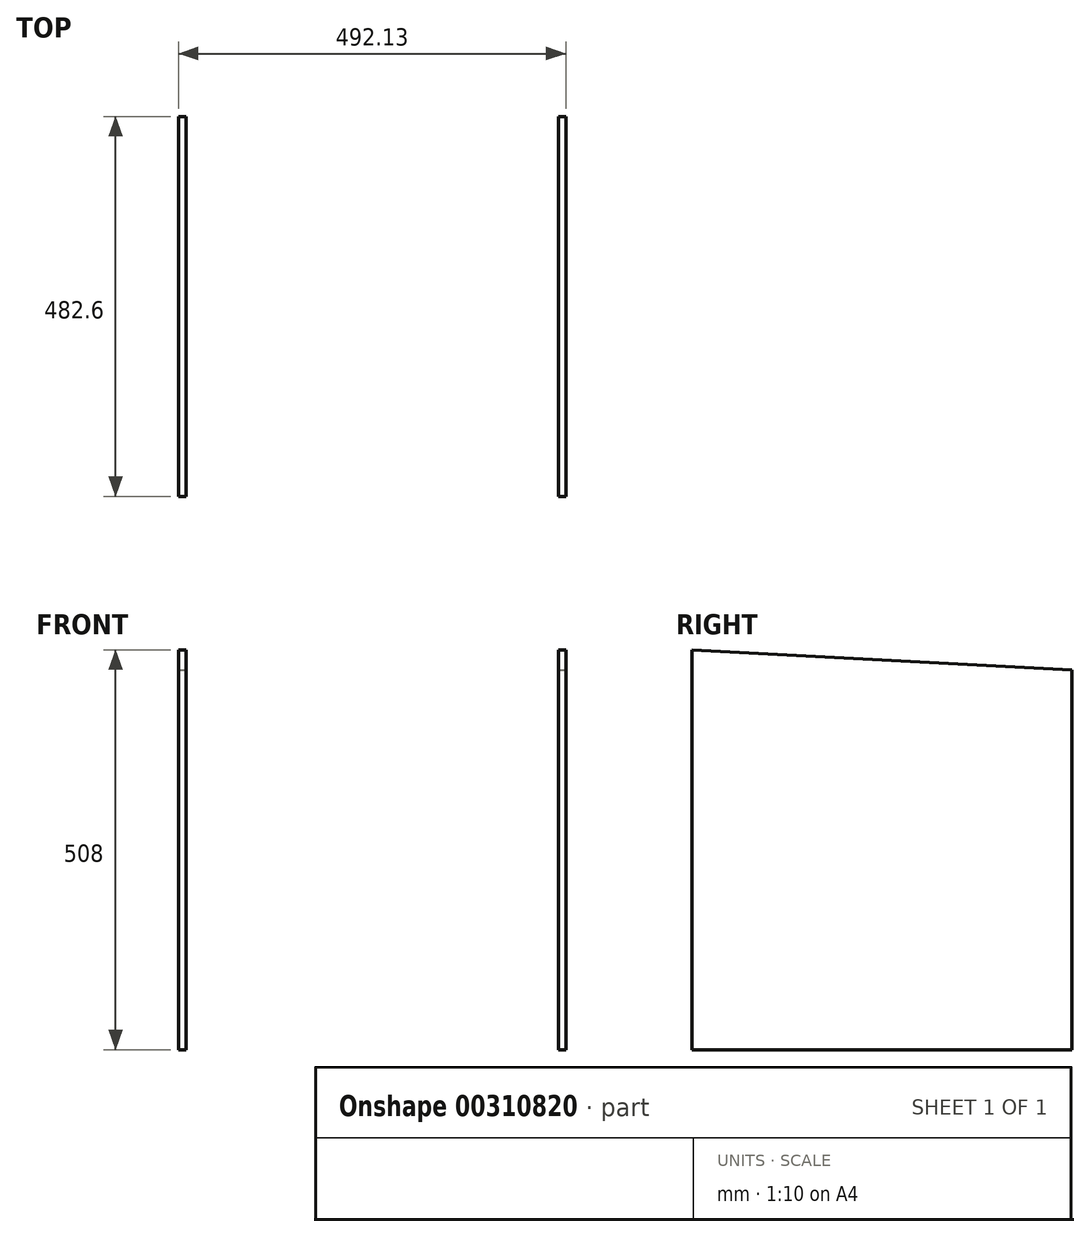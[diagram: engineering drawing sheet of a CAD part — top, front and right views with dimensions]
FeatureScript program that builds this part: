
annotation { "Feature Type Name" : "Feature", "Feature Type Description" : "" }
export const myFeature = defineFeature(function(context is Context, id is Id, definition is map)
    precondition{}
    {
        {
            var Q0;
            Q0=qCreatedBy(makeId("Right.planeOp"),FACE);
            var sketch = newSketch(context, id + "F0", { "sketchPlane" : qUnion([Q0])});
            skLineSegment(sketch, "E0.top", {"start": v(-920.3, -120.27) * mm, "end": v(-437.7, -120.27) * mm});
            skLineSegment(sketch, "E0.left", {"start": v(-920.3, 362.33) * mm, "end": v(-920.3, -120.27) * mm});
            skLineSegment(sketch, "E1", {"start": v(-437.7, -120.27) * mm, "end": v(-437.7, 387.73) * mm});
            skLineSegment(sketch, "E2", {"start": v(-920.3, 362.33) * mm, "end": v(-437.7, 387.73) * mm});
            skSolve(sketch);
        }
        {
            var Q0;
            Q0=makeQuery(id+"F0.imprint","IMPRINT",FACE,{"disambiguationData":[TD([[makeQuery(id+"F0.imprint","IMPRINT",EDGE,{"derivedFrom":sQuery(id+"F0.wireOp",EDGE,"E0.top")}),1.0]])]});
            extrude(context, id + "F1", {"entities" : qUnion([Q0]), "depth" : 9.52 * mm});
        }
        {
            var Q0;
            Q0=makeQuery(id+"F1.opExtrude","SWEPT_BODY",BODY,{"disambiguationData":[OSD([sQuery(id+"F0.wireOp",EDGE,"E0.top"),sQuery(id+"F0.wireOp",EDGE,"E0.left"),sQuery(id+"F0.wireOp",EDGE,"E1"),sQuery(id+"F0.wireOp",EDGE,"E2")])]});
            transform(context, id + "F2", {"entities" : qUnion([Q0]), "transformType" : TransformType.TRANSLATION_3D, "dx" : 482.6 * mm, "dy" : 0 * mm, "dz" : 0 * mm, "makeCopy" : true});
        }
        {
            var Q0;
            Q0=makeQuery(id+"F2.opPattern","COPY",BODY,{"derivedFrom":makeQuery(id+"F1.opExtrude","SWEPT_BODY",BODY,{"disambiguationData":[OSD([sQuery(id+"F0.wireOp",EDGE,"E0.top"),sQuery(id+"F0.wireOp",EDGE,"E0.left"),sQuery(id+"F0.wireOp",EDGE,"E1"),sQuery(id+"F0.wireOp",EDGE,"E2")])]}),"instanceName":"1"});
            var Q1;
            Q1=makeQuery(id+"F2.opPattern","COPY",EDGE,{"derivedFrom":makeQuery(id+"F1.opExtrude","CAP_EDGE",EDGE,{"disambiguationData":[OSD([sQuery(id+"F0.wireOp",EDGE,"E0.left")])],"isStart":false}),"instanceName":"1"});
            transform(context, id + "F3", {"entities" : qUnion([Q0]), "transformType" : TransformType.ROTATION, "transformAxis" : qUnion([Q1]), "angle" : 180 * degree, "makeCopy" : false});
        }
        {
            var Q0;
            Q0=makeQuery(id+"F1.opExtrude","SWEPT_BODY",BODY,{"disambiguationData":[OSD([sQuery(id+"F0.wireOp",EDGE,"E0.top"),sQuery(id+"F0.wireOp",EDGE,"E0.left"),sQuery(id+"F0.wireOp",EDGE,"E1"),sQuery(id+"F0.wireOp",EDGE,"E2")])]});
            var Q1;
            Q1=makeQuery(id+"F1.opExtrude","CAP_EDGE",EDGE,{"disambiguationData":[OSD([sQuery(id+"F0.wireOp",EDGE,"E0.left")])],"isStart":false});
            transform(context, id + "F4", {"entities" : qUnion([Q0]), "transformType" : TransformType.ROTATION, "transformAxis" : qUnion([Q1]), "angle" : 180 * degree, "makeCopy" : false});
        }
    });
